# Revit family: Pipe-Clamp-Atkore-Thinwall-Conduit-P1427
name_source: partatom
category: Specialty Equipment
revit_build: Autodesk Revit MEP 2012 (Build: 20110309_2315(x64)
units: mm (PartAtom-declared; Revit-internal decimal feet)

## types (1)
- P1427
    04 CSI = 26 05 48
    95 CSI = 16070
    Assembly Code = D5090300
    Conduit Size = 19.1 mm  [stored 0.062664 ft]
    Description = Pipe Clamps For Thin Wall Conduit
    Load Capacity Note = Visit the product page for load application and capacity.
    Manufacturer = Unistrut by Atkore International
    Manufacturer Fax = 708-339-7814
    Material = Multiple Options - See Catalog
    Model = P1427
    Outer Diameter = 23.4 mm  [stored 0.0767717 ft]
    Overall Depth = 31.93 mm  [stored 0.104757 ft]
    Overall Height = 57.55 mm  [stored 0.188812 ft]
    Overall Width = 26.79 mm  [stored 0.0878937 ft]
    Part Number = P1427
    Part Type = Clamp
    Subcategory = Pipe Clamps
    Thickness Gauge = 1.5 mm  [stored 0.00492126 ft]
    URL = http://unistrut.us
    Unit = Metal - Aluminum - Atkore - Electro - Galvanized

note: [stored X ft] marks values corroborated as IEEE doubles in the binary element streams (Revit-internal decimal feet)

## geometry (parser evidence)
native form markers: Blend x4, Sweep x3
no freeform markers — native parametric forms only
